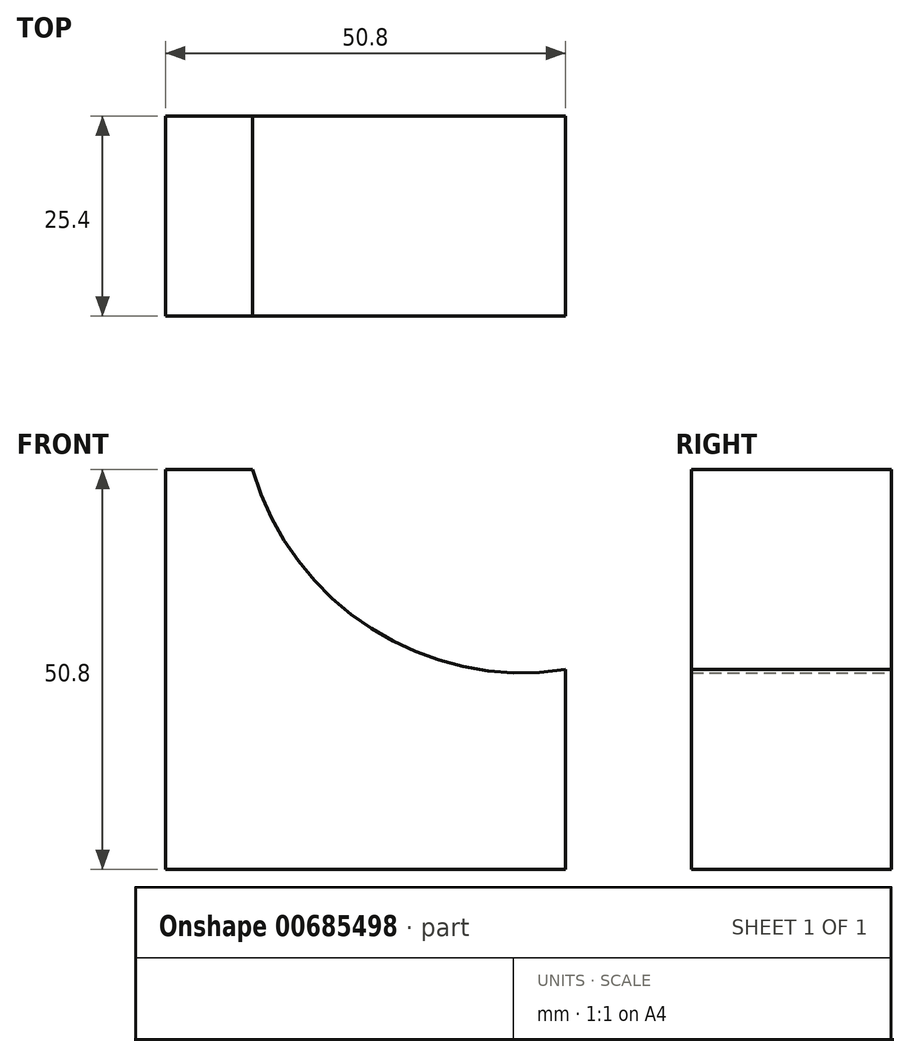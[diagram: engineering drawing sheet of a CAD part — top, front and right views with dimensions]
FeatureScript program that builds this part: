
annotation { "Feature Type Name" : "Feature", "Feature Type Description" : "" }
export const myFeature = defineFeature(function(context is Context, id is Id, definition is map)
    precondition{}
    {
        {
            var Q0;
            Q0=qCreatedBy(makeId("Front.planeOp"),FACE);
            var sketch = newSketch(context, id + "F0", { "sketchPlane" : qUnion([Q0])});
            skLineSegment(sketch, "E0", {"start": v(-53.18, 57.96) * mm, "end": v(-53.18, 7.16) * mm});
            skLineSegment(sketch, "E1", {"start": v(-53.18, 7.16) * mm, "end": v(-2.38, 7.16) * mm});
            skLineSegment(sketch, "E2", {"start": v(-2.38, 7.16) * mm, "end": v(-2.38, 32.56) * mm});
            skLineSegment(sketch, "E3", {"start": v(-53.18, 57.96) * mm, "end": v(-42.1, 57.96) * mm});
            skArc(sketch, "E4", {"start": v(-42.1, 57.96) * mm, "mid": v(-27.05, 37.75) * mm, "end": v(-2.38, 32.56) * mm});
            skSolve(sketch);
        }
        {
            var Q0;
            Q0 = qSketchRegion(id + "F0", true);
            extrude(context, id + "F1", {"entities" : qUnion([Q0]), "depth" : 25.4 * mm, "offsetDistance" : 25.4 * mm});
        }
    });
